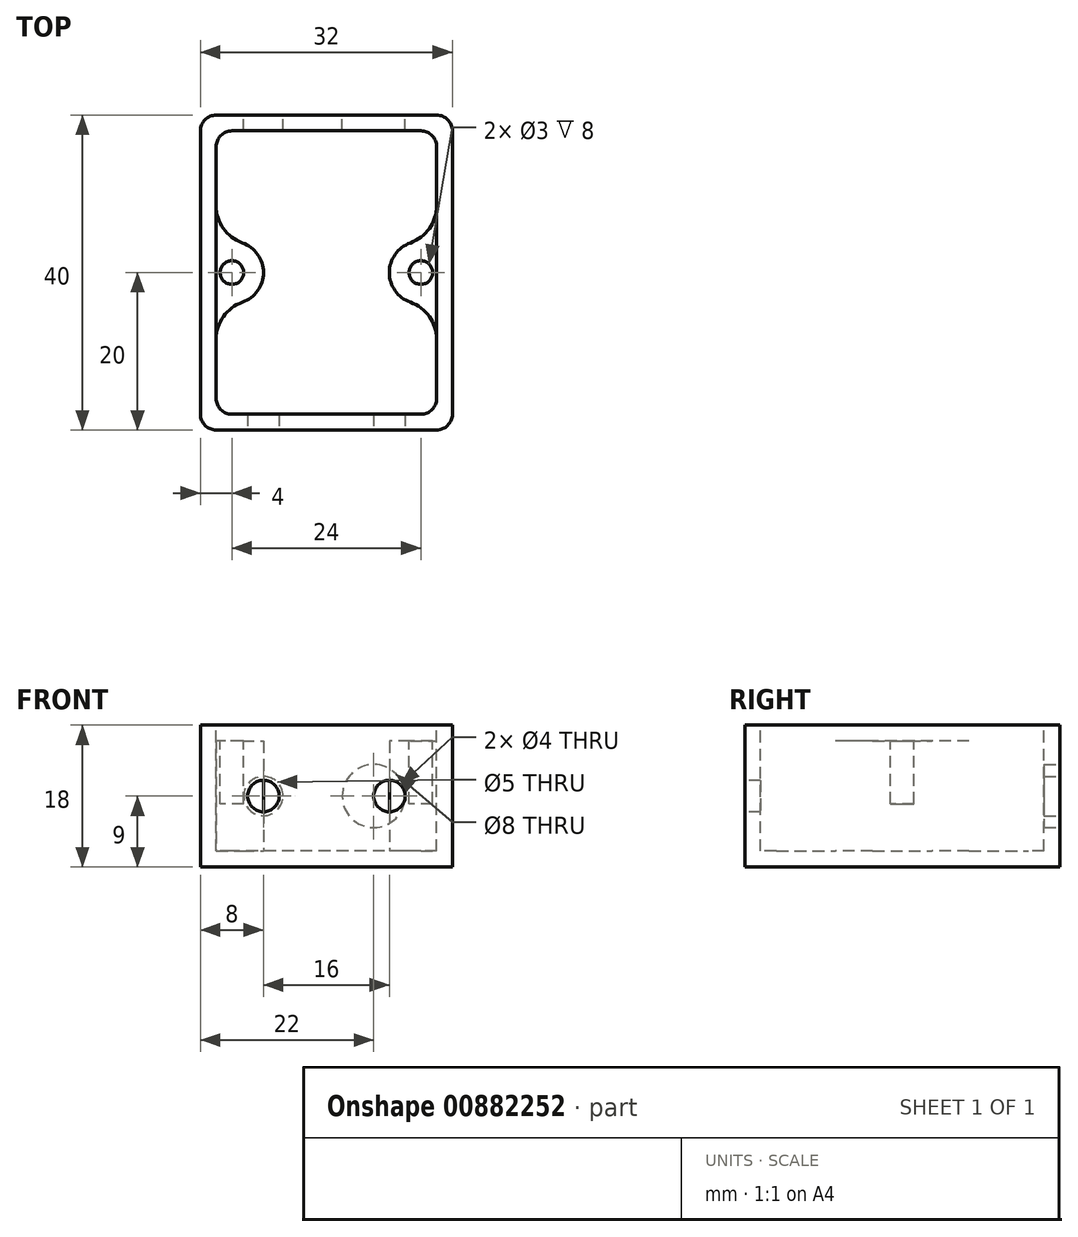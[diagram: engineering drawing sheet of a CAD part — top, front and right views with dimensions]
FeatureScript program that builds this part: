
annotation { "Feature Type Name" : "Feature", "Feature Type Description" : "" }
export const myFeature = defineFeature(function(context is Context, id is Id, definition is map)
    precondition{}
    {
        {
            var Q0;
            Q0=qCreatedBy(makeId("Top.planeOp"),FACE);
            var sketch = newSketch(context, id + "F0", { "sketchPlane" : qUnion([Q0])});
            skLineSegment(sketch, "E0.bottom", {"start": v(16, -20) * mm, "end": v(-16, -20) * mm});
            skLineSegment(sketch, "E0.top", {"start": v(16, 20) * mm, "end": v(-16, 20) * mm});
            skLineSegment(sketch, "E0.left", {"start": v(16, -20) * mm, "end": v(16, 20) * mm});
            skLineSegment(sketch, "E0.right", {"start": v(-16, -20) * mm, "end": v(-16, 20) * mm});
            skPoint(sketch, "E0.middle", {"position": v(0, 0) * mm});
            skSolve(sketch);
        }
        {
            var Q0;
            Q0=makeQuery(id+"F0.imprint","IMPRINT",FACE,{"disambiguationData":[TD([[makeQuery(id+"F0.imprint","IMPRINT",EDGE,{"derivedFrom":sQuery(id+"F0.wireOp",EDGE,"E0.bottom")}),-1.0]])]});
            extrude(context, id + "F1", {"entities" : qUnion([Q0]), "depth" : 18 * mm, "offsetDistance" : 25 * mm});
        }
        {
            var Q0;
            Q0=makeQuery(id+"F1.opExtrude","CAP_FACE",FACE,{"disambiguationData":[OSD([sQuery(id+"F0.wireOp",EDGE,"E0.bottom"),sQuery(id+"F0.wireOp",EDGE,"E0.top"),sQuery(id+"F0.wireOp",EDGE,"E0.left"),sQuery(id+"F0.wireOp",EDGE,"E0.right")])],"isStart":false});
            var sketch = newSketch(context, id + "F2", { "sketchPlane" : qUnion([Q0])});
            skLineSegment(sketch, "E1.bottom", {"start": v(14, -18) * mm, "end": v(-14, -18) * mm});
            skLineSegment(sketch, "E1.top", {"start": v(14, 18) * mm, "end": v(-14, 18) * mm});
            skLineSegment(sketch, "E1.left", {"start": v(14, -18) * mm, "end": v(14, 18) * mm});
            skLineSegment(sketch, "E1.right", {"start": v(-14, -18) * mm, "end": v(-14, 18) * mm});
            skPoint(sketch, "E1.middle", {"position": v(0, 0) * mm});
            skSolve(sketch);
        }
        {
            var Q0;
            Q0=makeQuery(id+"F2.imprint","IMPRINT",FACE,{"disambiguationData":[TD([[makeQuery(id+"F2.imprint","IMPRINT",EDGE,{"derivedFrom":sQuery(id+"F2.wireOp",EDGE,"E1.bottom")}),-1.0]])]});
            extrude(context, id + "F3", {"entities" : qUnion([Q0]), "operationType" : NewBodyOperationType.REMOVE, "oppositeDirection" : true, "depth" : 16 * mm, "offsetDistance" : 25 * mm});
        }
        {
            var Q0;
            Q0=makeQuery(id+"F1.opExtrude","SWEPT_FACE",FACE,{"disambiguationData":[OSD([sQuery(id+"F0.wireOp",EDGE,"E0.top")])]});
            var sketch = newSketch(context, id + "F4", { "sketchPlane" : qUnion([Q0])});
            skCircle(sketch, "E2", {"center": v(-6, 9) * mm, "radius": 4 * mm});
            skPoint(sketch, "E2.centerSnap0", {"position": v(-16, 9) * mm});
            skCircle(sketch, "E3", {"center": v(8, 9) * mm, "radius": 2.5 * mm});
            skSolve(sketch);
        }
        {
            var Q0;
            Q0=makeQuery(id+"F4.imprint","IMPRINT",FACE,{"disambiguationData":[TD([[makeQuery(id+"F4.imprint","IMPRINT",EDGE,{"derivedFrom":sQuery(id+"F4.wireOp",EDGE,"E2")}),1.0]])]});
            var Q1;
            Q1=makeQuery(id+"F4.imprint","IMPRINT",FACE,{"disambiguationData":[TD([[makeQuery(id+"F4.imprint","IMPRINT",EDGE,{"derivedFrom":sQuery(id+"F4.wireOp",EDGE,"E3")}),1.0]])]});
            extrude(context, id + "F5", {"entities" : qUnion([Q0, Q1]), "operationType" : NewBodyOperationType.REMOVE, "oppositeDirection" : true, "depth" : 3 * mm, "offsetDistance" : 25 * mm});
        }
        {
            var Q0;
            Q0=makeQuery(id+"F1.opExtrude","SWEPT_FACE",FACE,{"disambiguationData":[OSD([sQuery(id+"F0.wireOp",EDGE,"E0.bottom")])]});
            var sketch = newSketch(context, id + "F6", { "sketchPlane" : qUnion([Q0])});
            skCircle(sketch, "E4", {"center": v(-8, 9) * mm, "radius": 2 * mm});
            skPoint(sketch, "E4.centerSnap0", {"position": v(-16, 9) * mm});
            skCircle(sketch, "E5", {"center": v(8, 9) * mm, "radius": 2 * mm});
            skPoint(sketch, "E5.centerSnap0", {"position": v(16, 9) * mm});
            skSolve(sketch);
        }
        {
            var Q0;
            Q0=makeQuery(id+"F6.imprint","IMPRINT",FACE,{"disambiguationData":[TD([[makeQuery(id+"F6.imprint","IMPRINT",EDGE,{"derivedFrom":sQuery(id+"F6.wireOp",EDGE,"E4")}),1.0]])]});
            var Q1;
            Q1=makeQuery(id+"F6.imprint","IMPRINT",FACE,{"disambiguationData":[TD([[makeQuery(id+"F6.imprint","IMPRINT",EDGE,{"derivedFrom":sQuery(id+"F6.wireOp",EDGE,"E5")}),1.0]])]});
            extrude(context, id + "F7", {"entities" : qUnion([Q0, Q1]), "operationType" : NewBodyOperationType.REMOVE, "oppositeDirection" : true, "depth" : 3 * mm, "offsetDistance" : 25 * mm});
        }
        {
            var Q0;
            Q0=makeQuery(id+"F3.boolean.opBoolean","COPY",FACE,{"derivedFrom":makeQuery(id+"F3.opExtrude","CAP_FACE",FACE,{"disambiguationData":[OSD([sQuery(id+"F2.wireOp",EDGE,"E1.bottom"),sQuery(id+"F2.wireOp",EDGE,"E1.top"),sQuery(id+"F2.wireOp",EDGE,"E1.left"),sQuery(id+"F2.wireOp",EDGE,"E1.right")])],"isStart":false})});
            var sketch = newSketch(context, id + "F8", { "sketchPlane" : qUnion([Q0])});
            skCircle(sketch, "E6", {"center": v(-12, 0) * mm, "radius": 4 * mm});
            skCircle(sketch, "E7", {"center": v(12, 0) * mm, "radius": 4 * mm});
            skSolve(sketch);
        }
        {
            var Q0;
            Q0 = qSketchRegion(id + "F8", true);
            extrude(context, id + "F9", {"entities" : qUnion([Q0]), "operationType" : NewBodyOperationType.ADD, "depth" : 14 * mm, "offsetDistance" : 25 * mm});
        }
        {
            var Q0;
            Q0=makeQuery(id+"F9.opExtrude","CAP_FACE",FACE,{"disambiguationData":[OSD([sQuery(id+"F8.wireOp",EDGE,"E7")])],"isStart":false});
            var sketch = newSketch(context, id + "F10", { "sketchPlane" : qUnion([Q0])});
            skCircle(sketch, "E8", {"center": v(12, 0) * mm, "radius": 1.5 * mm});
            skCircle(sketch, "E9", {"center": v(-12, 0) * mm, "radius": 1.5 * mm});
            skSolve(sketch);
        }
        {
            var Q0;
            Q0=makeQuery(id+"F10.imprint","IMPRINT",FACE,{"disambiguationData":[TD([[makeQuery(id+"F10.imprint","IMPRINT",EDGE,{"derivedFrom":sQuery(id+"F10.wireOp",EDGE,"E9")}),1.0]])]});
            var Q1;
            Q1=makeQuery(id+"F10.imprint","IMPRINT",FACE,{"disambiguationData":[TD([[makeQuery(id+"F10.imprint","IMPRINT",EDGE,{"derivedFrom":sQuery(id+"F10.wireOp",EDGE,"E8")}),1.0]])]});
            extrude(context, id + "F11", {"entities" : qUnion([Q0, Q1]), "operationType" : NewBodyOperationType.REMOVE, "oppositeDirection" : true, "depth" : 8 * mm, "offsetDistance" : 25 * mm});
        }
        {
            var Q0;
            Q0=makeQuery(id+"F9.boolean.opBoolean","INTERSECT",EDGE,{"disambiguationData":[OD(0.0)],"derivedFrom":[makeQuery(id+"F3.boolean.opBoolean","COPY",FACE,{"derivedFrom":makeQuery(id+"F3.opExtrude","SWEPT_FACE",FACE,{"disambiguationData":[OSD([sQuery(id+"F2.wireOp",EDGE,"E1.left")])]})}),makeQuery(id+"F9.opExtrude","SWEPT_FACE",FACE,{"disambiguationData":[OSD([sQuery(id+"F8.wireOp",EDGE,"E7")])]})]});
            var Q1;
            Q1=makeQuery(id+"F9.boolean.opBoolean","INTERSECT",EDGE,{"disambiguationData":[OD(1.0)],"derivedFrom":[makeQuery(id+"F3.boolean.opBoolean","COPY",FACE,{"derivedFrom":makeQuery(id+"F3.opExtrude","SWEPT_FACE",FACE,{"disambiguationData":[OSD([sQuery(id+"F2.wireOp",EDGE,"E1.left")])]})}),makeQuery(id+"F9.opExtrude","SWEPT_FACE",FACE,{"disambiguationData":[OSD([sQuery(id+"F8.wireOp",EDGE,"E7")])]})]});
            var Q2;
            Q2=makeQuery(id+"F9.boolean.opBoolean","INTERSECT",EDGE,{"disambiguationData":[OD(1.0)],"derivedFrom":[makeQuery(id+"F3.boolean.opBoolean","COPY",FACE,{"derivedFrom":makeQuery(id+"F3.opExtrude","SWEPT_FACE",FACE,{"disambiguationData":[OSD([sQuery(id+"F2.wireOp",EDGE,"E1.right")])]})}),makeQuery(id+"F9.opExtrude","SWEPT_FACE",FACE,{"disambiguationData":[OSD([sQuery(id+"F8.wireOp",EDGE,"E6")])]})]});
            var Q3;
            Q3=makeQuery(id+"F9.boolean.opBoolean","INTERSECT",EDGE,{"disambiguationData":[OD(0.0)],"derivedFrom":[makeQuery(id+"F3.boolean.opBoolean","COPY",FACE,{"derivedFrom":makeQuery(id+"F3.opExtrude","SWEPT_FACE",FACE,{"disambiguationData":[OSD([sQuery(id+"F2.wireOp",EDGE,"E1.right")])]})}),makeQuery(id+"F9.opExtrude","SWEPT_FACE",FACE,{"disambiguationData":[OSD([sQuery(id+"F8.wireOp",EDGE,"E6")])]})]});
            fillet(context, id + "F12", {"entities" : qUnion([Q0, Q1, Q2, Q3]), "radius" : 5 * mm, "tangentPropagation" : true, "allowEdgeOverflow" : false});
        }
        {
            var Q0;
            Q0=makeQuery(id+"F3.boolean.opBoolean","COPY",EDGE,{"derivedFrom":makeQuery(id+"F3.opExtrude","SWEPT_EDGE",EDGE,{"disambiguationData":[OSD([sQuery(id+"F2.wireOp",EDGE,"E1.bottom"),sQuery(id+"F2.wireOp",EDGE,"E1.right")])]})});
            var Q1;
            Q1=makeQuery(id+"F3.boolean.opBoolean","COPY",EDGE,{"derivedFrom":makeQuery(id+"F3.opExtrude","SWEPT_EDGE",EDGE,{"disambiguationData":[OSD([sQuery(id+"F2.wireOp",EDGE,"E1.bottom"),sQuery(id+"F2.wireOp",EDGE,"E1.left")])]})});
            var Q2;
            Q2=makeQuery(id+"F3.boolean.opBoolean","COPY",EDGE,{"derivedFrom":makeQuery(id+"F3.opExtrude","SWEPT_EDGE",EDGE,{"disambiguationData":[OSD([sQuery(id+"F2.wireOp",EDGE,"E1.top"),sQuery(id+"F2.wireOp",EDGE,"E1.left")])]})});
            var Q3;
            Q3=makeQuery(id+"F3.boolean.opBoolean","COPY",EDGE,{"derivedFrom":makeQuery(id+"F3.opExtrude","SWEPT_EDGE",EDGE,{"disambiguationData":[OSD([sQuery(id+"F2.wireOp",EDGE,"E1.top"),sQuery(id+"F2.wireOp",EDGE,"E1.right")])]})});
            fillet(context, id + "F13", {"entities" : qUnion([Q0, Q1, Q2, Q3]), "radius" : 2 * mm, "tangentPropagation" : true, "allowEdgeOverflow" : false});
        }
        {
            var Q0;
            Q0=makeQuery(id+"F1.opExtrude","SWEPT_EDGE",EDGE,{"disambiguationData":[OSD([sQuery(id+"F0.wireOp",EDGE,"E0.top"),sQuery(id+"F0.wireOp",EDGE,"E0.left")])]});
            var Q1;
            Q1=makeQuery(id+"F1.opExtrude","SWEPT_EDGE",EDGE,{"disambiguationData":[OSD([sQuery(id+"F0.wireOp",EDGE,"E0.bottom"),sQuery(id+"F0.wireOp",EDGE,"E0.left")])]});
            var Q2;
            Q2=makeQuery(id+"F1.opExtrude","SWEPT_EDGE",EDGE,{"disambiguationData":[OSD([sQuery(id+"F0.wireOp",EDGE,"E0.bottom"),sQuery(id+"F0.wireOp",EDGE,"E0.right")])]});
            var Q3;
            Q3=makeQuery(id+"F1.opExtrude","SWEPT_EDGE",EDGE,{"disambiguationData":[OSD([sQuery(id+"F0.wireOp",EDGE,"E0.top"),sQuery(id+"F0.wireOp",EDGE,"E0.right")])]});
            fillet(context, id + "F14", {"entities" : qUnion([Q0, Q1, Q2, Q3]), "radius" : 2 * mm, "tangentPropagation" : true, "allowEdgeOverflow" : false});
        }
    });
